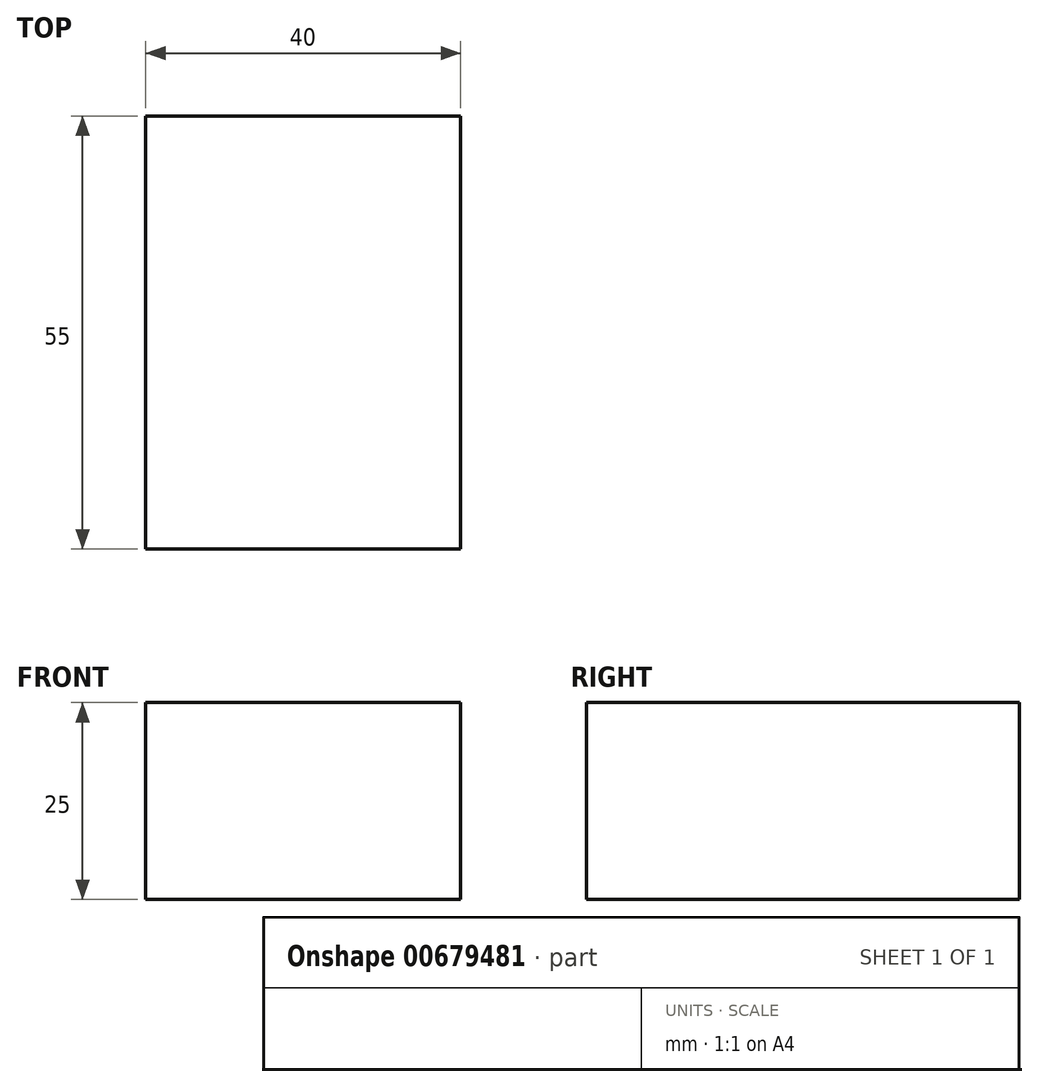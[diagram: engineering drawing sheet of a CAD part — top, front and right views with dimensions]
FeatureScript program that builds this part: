
annotation { "Feature Type Name" : "Feature", "Feature Type Description" : "" }
export const myFeature = defineFeature(function(context is Context, id is Id, definition is map)
    precondition{}
    {
        {
            var Q0;
            Q0=qCreatedBy(makeId("Top.planeOp"),FACE);
            var sketch = newSketch(context, id + "F0", { "sketchPlane" : qUnion([Q0])});
            skLineSegment(sketch, "E0.bottom", {"start": v(-20, -27.5) * mm, "end": v(20, -27.5) * mm});
            skLineSegment(sketch, "E0.top", {"start": v(-20, 27.5) * mm, "end": v(20, 27.5) * mm});
            skLineSegment(sketch, "E0.left", {"start": v(-20, -27.5) * mm, "end": v(-20, 27.5) * mm});
            skLineSegment(sketch, "E0.right", {"start": v(20, -27.5) * mm, "end": v(20, 27.5) * mm});
            skLineSegment(sketch, "E1", {"start": v(0, -46.82) * mm, "end": v(0, 52.48) * mm, "construction": true});
            skLineSegment(sketch, "E2", {"start": v(-40.27, 0) * mm, "end": v(49.1, 0) * mm, "construction": true});
            skSolve(sketch);
        }
        {
            var Q0;
            Q0=makeQuery(id+"F0.imprint","IMPRINT",FACE,{"disambiguationData":[TD([[makeQuery(id+"F0.imprint","IMPRINT",EDGE,{"derivedFrom":sQuery(id+"F0.wireOp",EDGE,"E0.bottom")}),1.0]])]});
            extrude(context, id + "F1", {"entities" : qUnion([Q0]), "depth" : 25 * mm, "offsetDistance" : 25 * mm});
        }
    });
